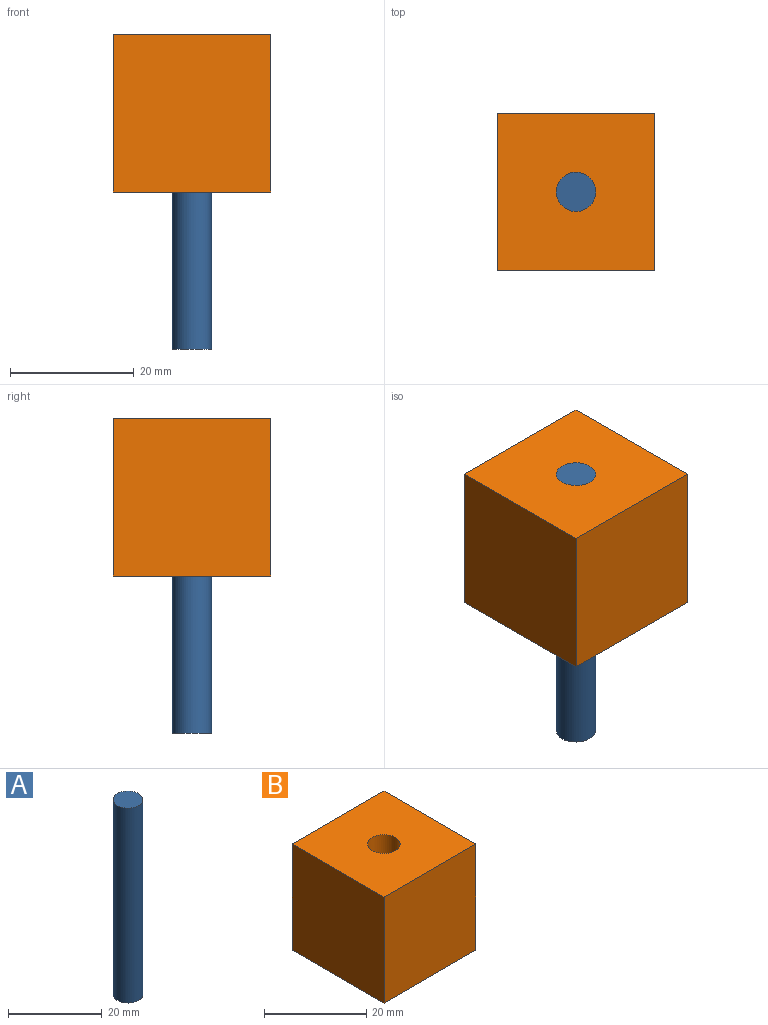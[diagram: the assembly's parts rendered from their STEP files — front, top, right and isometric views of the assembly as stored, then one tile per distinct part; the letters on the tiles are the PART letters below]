
ASSEMBLY  parts=2 mates=1
PART A: 3 faces, bbox 6.4x6.4x50.8 mm
  f0: cylinder r=3.17mm len=50.8mm, axis (0,0,-1), area 1013.4mm2, adj f1,f2
  f1: plane 6.35x6.35mm, normal (0,0,1), area 31.7mm2, adj f0
  f2: plane 6.35x6.35mm, normal (0,0,-1), area 31.7mm2, adj f0
PART B: 7 faces, bbox 25.4x25.4x25.4 mm
  f0: plane 25.4x25.4mm, normal (0,-1,0), area 645.2mm2, adj f1,f4,f5,f6
  f1: plane 25.4x25.4mm, normal (1,0,0), area 645.2mm2, adj f0,f2,f5,f6
  f2: plane 25.4x25.4mm, normal (0,1,0), area 645.2mm2, adj f1,f4,f5,f6
  f3: cylinder r=3.17mm len=25.4mm, axis (0,0,-1), area 506.7mm2, adj f5,f6
  f4: plane 25.4x25.4mm, normal (-1,0,0), area 645.2mm2, adj f0,f2,f5,f6
  f5: plane 25.4x25.4mm, normal (0,0,1), area 613.5mm2, adj f0,f1,f2,f3,f4
  f6: plane 25.4x25.4mm, normal (0,0,-1), area 613.5mm2, adj f0,f1,f2,f3,f4
PLACE A t=(-15.9,-10.47,-18.58)mm
PLACE B t=(44.61,-18.07,6.82)mm
MATE slider A.f0 <-> B.f3  axis (0,0,1) through (8.23,24.76,32.22)mm
